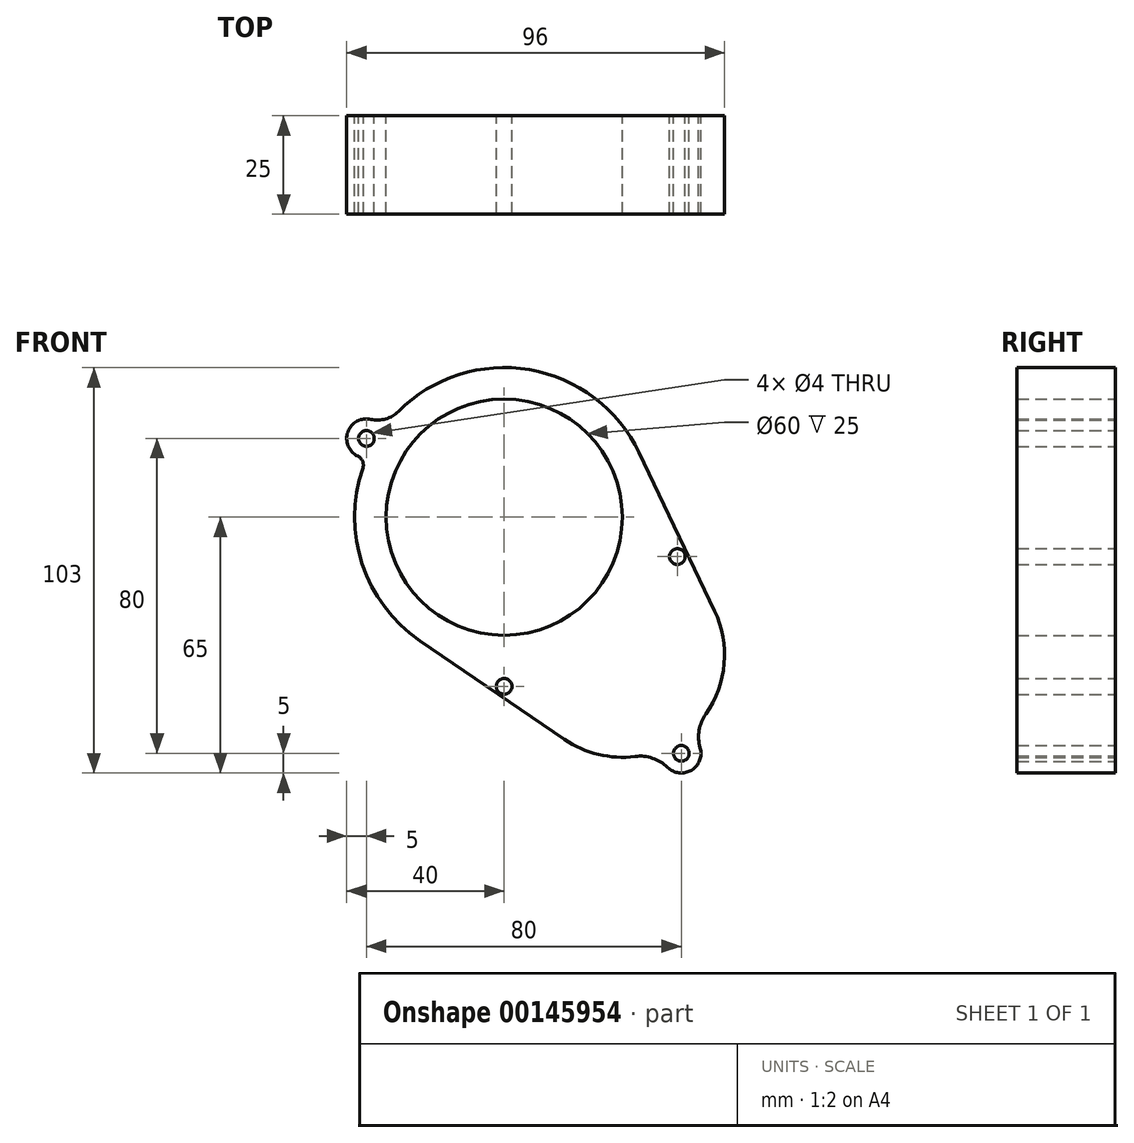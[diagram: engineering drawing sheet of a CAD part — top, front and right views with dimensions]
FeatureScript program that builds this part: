
annotation { "Feature Type Name" : "Feature", "Feature Type Description" : "" }
export const myFeature = defineFeature(function(context is Context, id is Id, definition is map)
    precondition{}
    {
        {
            var Q0;
            Q0=qCreatedBy(makeId("Front.planeOp"),FACE);
            var sketch = newSketch(context, id + "F0", { "sketchPlane" : qUnion([Q0])});
            skArc(sketch, "E0", {"start": v(-35.9, 12.43) * mm, "mid": v(-36.08, -11.93) * mm, "end": v(-21.42, -31.39) * mm});
            skCircle(sketch, "E1", {"center": v(0, 0) * mm, "radius": 30 * mm});
            skCircle(sketch, "E2", {"center": v(44, -10) * mm, "radius": 2 * mm});
            skCircle(sketch, "E3", {"center": v(45, -60) * mm, "radius": 2 * mm});
            skCircle(sketch, "E4", {"center": v(-35, 20) * mm, "radius": 2 * mm});
            skArc(sketch, "E5", {"start": v(15.34, -56.48) * mm, "mid": v(23.9, -60.28) * mm, "end": v(33.25, -60.8) * mm});
            skCircle(sketch, "E6", {"center": v(0, -43) * mm, "radius": 2 * mm});
            skArc(sketch, "E7", {"start": v(-33.87, 24.87) * mm, "mid": v(-39.71, 21.67) * mm, "end": v(-37.18, 15.5) * mm});
            skPoint(sketch, "E8", {"position": v(-40, 20) * mm});
            skArc(sketch, "E9", {"start": v(-33.87, 24.87) * mm, "mid": v(-30.1, 24.96) * mm, "end": v(-26.87, 26.87) * mm});
            skArc(sketch, "E10", {"start": v(-35.9, 12.43) * mm, "mid": v(-35.96, 14.2) * mm, "end": v(-37.18, 15.5) * mm});
            skLineSegment(sketch, "E11", {"start": v(-21.42, -31.39) * mm, "end": v(15.34, -56.48) * mm});
            skLineSegment(sketch, "E12", {"start": v(34.3, 16.37) * mm, "end": v(53.46, -23.8) * mm});
            skArc(sketch, "E13", {"start": v(41.5, -63.57) * mm, "mid": v(47.57, -64.29) * mm, "end": v(49.8, -58.6) * mm});
            skArc(sketch, "E14.trimOffspring", {"start": v(34.3, 16.37) * mm, "mid": v(6.43, 37.45) * mm, "end": v(-26.87, 26.87) * mm});
            skArc(sketch, "E15", {"start": v(51.23, -50) * mm, "mid": v(49.53, -54.14) * mm, "end": v(49.8, -58.6) * mm});
            skArc(sketch, "E16", {"start": v(41.5, -63.57) * mm, "mid": v(37.7, -61.24) * mm, "end": v(33.25, -60.8) * mm});
            skArc(sketch, "E17.trimOffspring", {"start": v(51.23, -50) * mm, "mid": v(55.9, -37.2) * mm, "end": v(53.46, -23.8) * mm});
            skSolve(sketch);
        }
        {
            var Q0;
            Q0 = qSketchRegion(id + "F0", true);
            extrude(context, id + "F1", {"entities" : qUnion([Q0]), "depth" : 25 * mm});
        }
    });
